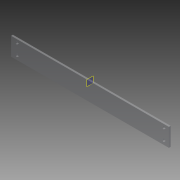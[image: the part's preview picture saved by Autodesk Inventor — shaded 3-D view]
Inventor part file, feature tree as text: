
AUTODESK INVENTOR PART (.ipt)
format: ipt  version: 2013 (Build 170138000, 138)  size: 83,456 bytes
history: native  units: in
note: dims shown in document units (in); Inventor stores cm internally (conversion verified against a paired STEP export)
features: sketch x2, extrude x1, hole x1, plane x1
ambient origin geometry x8: Origin, YZ Plane, XZ Plane, XY Plane, X Axis, Y Axis, Z Axis, Center Point
bodies: Solid1 (feature_tree)
feature tree (5):
  extrude  "Extrusion1"  Depth=2.5in
  hole  "Hole1"  [1 undecoded]
  plane  "Work Plane1"
  sketch  "Sketch1"  dims[d0=21.75in d1=2.5in]
  sketch  "Sketch2"  dims[d2=0.25in d3=0.0in d4=0.75in d5=0.5in d6=2.0in d8=21.0in d9=0.31in d10=0.75in d11=0.375in d12=0.25in d13=0.5635in d14=1.0in d15=0.8108in]
note: 1 required parameter value undecoded (feature->parameter linkage not recoverable at this tier; creation-order binding heuristic only, values carry confidence <= 0.55)
